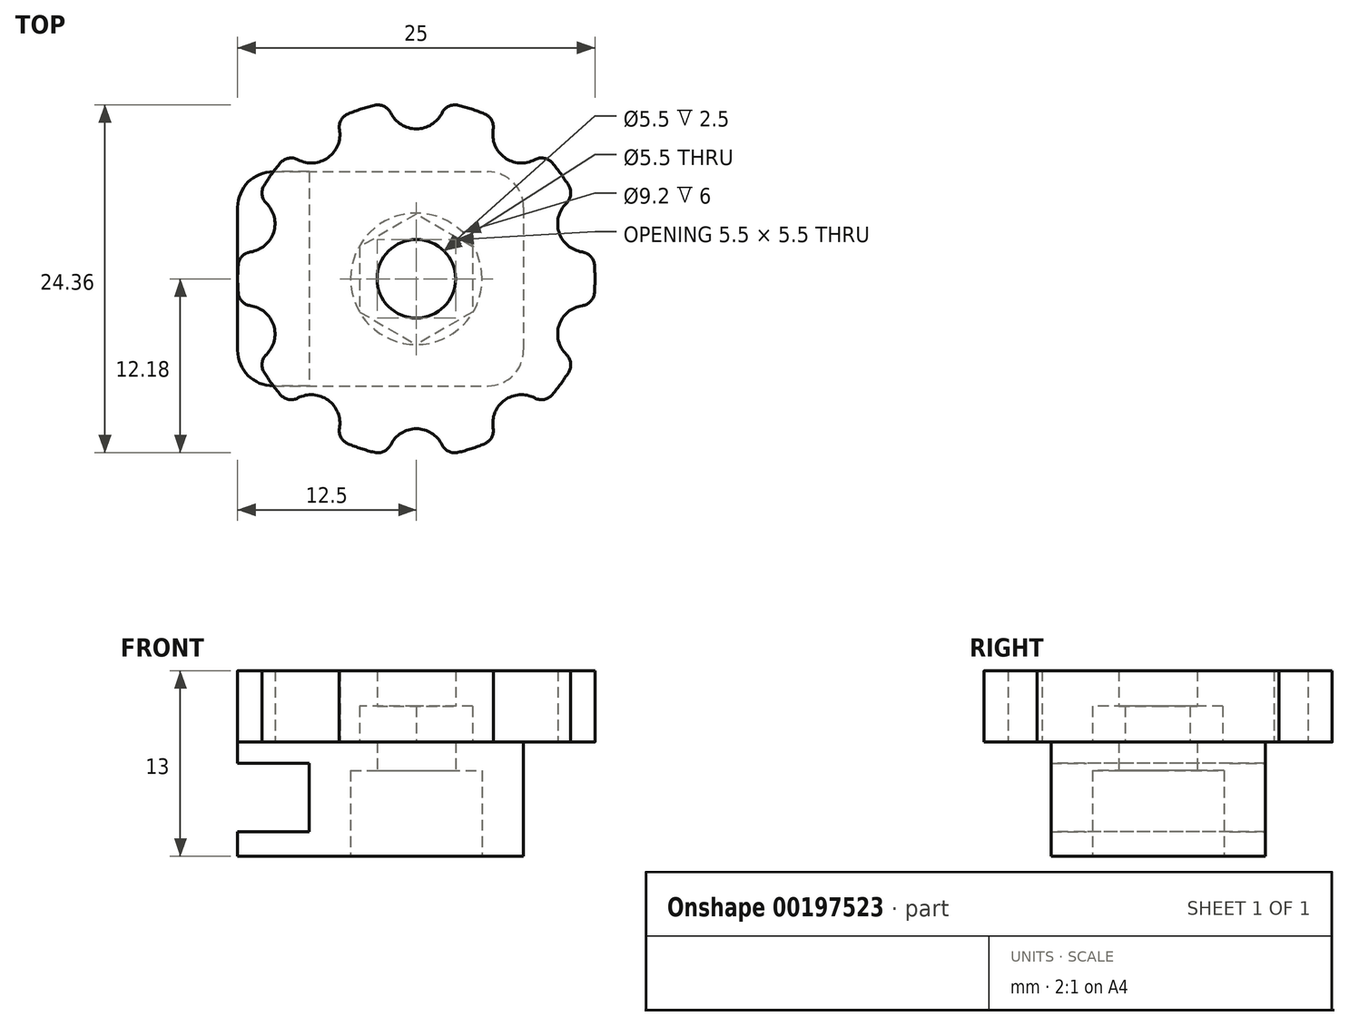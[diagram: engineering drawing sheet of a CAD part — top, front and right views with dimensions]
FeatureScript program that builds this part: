
annotation { "Feature Type Name" : "Feature", "Feature Type Description" : "" }
export const myFeature = defineFeature(function(context is Context, id is Id, definition is map)
    precondition{}
    {
        {
            var Q0;
            Q0=qCreatedBy(makeId("Top.planeOp"),FACE);
            var sketch = newSketch(context, id + "F0", { "sketchPlane" : qUnion([Q0])});
            skLineSegment(sketch, "E0.bottom", {"start": v(-12.5, 7.5) * mm, "end": v(7.5, 7.5) * mm});
            skLineSegment(sketch, "E0.top", {"start": v(-12.5, -7.5) * mm, "end": v(7.5, -7.5) * mm});
            skLineSegment(sketch, "E0.left", {"start": v(-12.5, 7.5) * mm, "end": v(-12.5, -7.5) * mm});
            skLineSegment(sketch, "E0.right", {"start": v(7.5, 7.5) * mm, "end": v(7.5, -7.5) * mm});
            skCircle(sketch, "E1", {"center": v(0, 0) * mm, "radius": 2.75 * mm});
            skSolve(sketch);
        }
        {
            var Q0;
            Q0=qSketchRegion(id+"F0",true);
            extrude(context, id + "F1", {"entities" : qUnion([Q0]), "depth" : 8 * mm});
        }
        {
            var Q0;
            Q0=makeQuery(id+"F1.opExtrude","SWEPT_FACE",FACE,{"disambiguationData":[OSD([sQuery(id+"F0.wireOp",EDGE,"E0.left")])]});
            var sketch = newSketch(context, id + "F2", { "sketchPlane" : qUnion([Q0])});
            skLineSegment(sketch, "E2.bottom", {"start": v(-7.5, 6.5) * mm, "end": v(7.5, 6.5) * mm});
            skLineSegment(sketch, "E2.top", {"start": v(-7.5, 1.7) * mm, "end": v(7.5, 1.7) * mm});
            skLineSegment(sketch, "E2.left", {"start": v(-7.5, 6.5) * mm, "end": v(-7.5, 1.7) * mm});
            skLineSegment(sketch, "E2.right", {"start": v(7.5, 6.5) * mm, "end": v(7.5, 1.7) * mm});
            skSolve(sketch);
        }
        {
            var Q0;
            Q0=qSketchRegion(id+"F2",true);
            extrude(context, id + "F3", {"entities" : qUnion([Q0]), "operationType" : NewBodyOperationType.REMOVE, "oppositeDirection" : true, "depth" : 5 * mm});
        }
        {
            var Q0;
            Q0=makeQuery(id+"F1.opExtrude","CAP_FACE",FACE,{"disambiguationData":[OSD([sQuery(id+"F0.wireOp",EDGE,"E0.bottom"),sQuery(id+"F0.wireOp",EDGE,"E0.top"),sQuery(id+"F0.wireOp",EDGE,"E0.left"),sQuery(id+"F0.wireOp",EDGE,"E0.right"),sQuery(id+"F0.wireOp",EDGE,"E1")])],"isStart":true});
            var sketch = newSketch(context, id + "F4", { "sketchPlane" : qUnion([Q0])});
            skCircle(sketch, "E3", {"center": v(0, 0) * mm, "radius": 4.6 * mm});
            skSolve(sketch);
        }
        {
            var Q0;
            Q0=qSketchRegion(id+"F4",true);
            extrude(context, id + "F5", {"entities" : qUnion([Q0]), "operationType" : NewBodyOperationType.REMOVE, "oppositeDirection" : true, "depth" : 6 * mm});
        }
        {
            var Q0;
            Q0=makeQuery(id+"F1.opExtrude","SWEPT_EDGE",EDGE,{"disambiguationData":[OSD([sQuery(id+"F0.wireOp",EDGE,"E0.top"),sQuery(id+"F0.wireOp",EDGE,"E0.right")])]});
            var Q1;
            Q1=makeQuery(id+"F1.opExtrude","SWEPT_EDGE",EDGE,{"disambiguationData":[OSD([sQuery(id+"F0.wireOp",EDGE,"E0.bottom"),sQuery(id+"F0.wireOp",EDGE,"E0.right")])]});
            fillet(context, id + "F6", {"entities" : qUnion([Q0, Q1]), "radius" : 2.5 * mm, "tangentPropagation" : true, "allowEdgeOverflow" : false});
        }
        {
            var Q0;
            {var subQ0=sQuery(id+"F0.wireOp",EDGE,"E0.left");var subQ1=sQuery(id+"F0.wireOp",EDGE,"E0.top");Q0=makeQuery(id+"F3.boolean.opBoolean","SPLIT",EDGE,{"disambiguationData":[TD([makeQuery(id+"F3.opExtrude","SWEPT_FACE",FACE,{"disambiguationData":[OSD([sQuery(id+"F2.wireOp",EDGE,"E2.top")])]})])],"derivedFrom":makeQuery(id+"F1.opExtrude","SWEPT_EDGE",EDGE,{"disambiguationData":[OSD([subQ1,subQ0])]})});}
            var Q1;
            {var subQ0=sQuery(id+"F0.wireOp",EDGE,"E0.left");var subQ1=sQuery(id+"F0.wireOp",EDGE,"E0.top");Q1=makeQuery(id+"F3.boolean.opBoolean","SPLIT",EDGE,{"disambiguationData":[TD([makeQuery(id+"F3.opExtrude","SWEPT_FACE",FACE,{"disambiguationData":[OSD([sQuery(id+"F2.wireOp",EDGE,"E2.bottom")])]})])],"derivedFrom":makeQuery(id+"F1.opExtrude","SWEPT_EDGE",EDGE,{"disambiguationData":[OSD([subQ1,subQ0])]})});}
            var Q2;
            {var subQ0=sQuery(id+"F0.wireOp",EDGE,"E0.bottom");var subQ1=sQuery(id+"F0.wireOp",EDGE,"E0.left");Q2=makeQuery(id+"F3.boolean.opBoolean","SPLIT",EDGE,{"disambiguationData":[TD([makeQuery(id+"F3.opExtrude","SWEPT_FACE",FACE,{"disambiguationData":[OSD([sQuery(id+"F2.wireOp",EDGE,"E2.top")])]})])],"derivedFrom":makeQuery(id+"F1.opExtrude","SWEPT_EDGE",EDGE,{"disambiguationData":[OSD([subQ0,subQ1])]})});}
            var Q3;
            {var subQ0=sQuery(id+"F0.wireOp",EDGE,"E0.bottom");var subQ1=sQuery(id+"F0.wireOp",EDGE,"E0.left");Q3=makeQuery(id+"F3.boolean.opBoolean","SPLIT",EDGE,{"disambiguationData":[TD([makeQuery(id+"F3.opExtrude","SWEPT_FACE",FACE,{"disambiguationData":[OSD([sQuery(id+"F2.wireOp",EDGE,"E2.bottom")])]})])],"derivedFrom":makeQuery(id+"F1.opExtrude","SWEPT_EDGE",EDGE,{"disambiguationData":[OSD([subQ0,subQ1])]})});}
            fillet(context, id + "F7", {"entities" : qUnion([Q0, Q1, Q2, Q3]), "radius" : 2.5 * mm, "tangentPropagation" : true, "allowEdgeOverflow" : false});
        }
        {
            var Q0;
            Q0=makeQuery(id+"F1.opExtrude","CAP_FACE",FACE,{"disambiguationData":[OSD([sQuery(id+"F0.wireOp",EDGE,"E0.bottom"),sQuery(id+"F0.wireOp",EDGE,"E0.top"),sQuery(id+"F0.wireOp",EDGE,"E0.left"),sQuery(id+"F0.wireOp",EDGE,"E0.right"),sQuery(id+"F0.wireOp",EDGE,"E1")])],"isStart":false});
            var sketch = newSketch(context, id + "F8", { "sketchPlane" : qUnion([Q0])});
            skArc(sketch, "E4", {"start": v(-2, 12.34) * mm, "mid": v(-3.86, 11.89) * mm, "end": v(-5.64, 11.16) * mm});
            skCircle(sketch, "E5.0", {"center": v(0, 0) * mm, "radius": 2.75 * mm});
            skArc(sketch, "E6", {"start": v(2, -12.34) * mm, "mid": v(0, -10.5) * mm, "end": v(-2, -12.34) * mm});
            skArc(sketch, "E7.1.0", {"start": v(8.87, -8.81) * mm, "mid": v(6.17, -8.5) * mm, "end": v(5.64, -11.16) * mm});
            skArc(sketch, "E7.2.0", {"start": v(12.35, -1.92) * mm, "mid": v(9.99, -3.24) * mm, "end": v(11.12, -5.7) * mm});
            skArc(sketch, "E7.3.0", {"start": v(11.12, 5.7) * mm, "mid": v(9.99, 3.24) * mm, "end": v(12.35, 1.92) * mm});
            skArc(sketch, "E7.4.0", {"start": v(5.64, 11.16) * mm, "mid": v(6.17, 8.5) * mm, "end": v(8.87, 8.81) * mm});
            skArc(sketch, "E7.5.0", {"start": v(-2, 12.34) * mm, "mid": v(0, 10.5) * mm, "end": v(2, 12.34) * mm});
            skArc(sketch, "E7.6.0", {"start": v(-8.87, 8.81) * mm, "mid": v(-6.17, 8.5) * mm, "end": v(-5.64, 11.16) * mm});
            skArc(sketch, "E7.7.0", {"start": v(-12.35, 1.92) * mm, "mid": v(-9.99, 3.24) * mm, "end": v(-11.12, 5.7) * mm});
            skArc(sketch, "E7.8.0", {"start": v(-11.12, -5.7) * mm, "mid": v(-9.99, -3.24) * mm, "end": v(-12.35, -1.92) * mm});
            skArc(sketch, "E7.9.0", {"start": v(-5.64, -11.16) * mm, "mid": v(-6.17, -8.5) * mm, "end": v(-8.87, -8.81) * mm});
            skArc(sketch, "E8.trimOffspring", {"start": v(5.64, 11.16) * mm, "mid": v(3.86, 11.89) * mm, "end": v(2, 12.34) * mm});
            skArc(sketch, "E9.trimOffspring", {"start": v(11.12, 5.7) * mm, "mid": v(10.11, 7.35) * mm, "end": v(8.87, 8.81) * mm});
            skArc(sketch, "E10.trimOffspring", {"start": v(12.35, -1.92) * mm, "mid": v(12.5, 0) * mm, "end": v(12.35, 1.92) * mm});
            skArc(sketch, "E11.trimOffspring", {"start": v(8.87, -8.81) * mm, "mid": v(10.11, -7.35) * mm, "end": v(11.12, -5.7) * mm});
            skArc(sketch, "E12.trimOffspring", {"start": v(2, -12.34) * mm, "mid": v(3.86, -11.89) * mm, "end": v(5.64, -11.16) * mm});
            skArc(sketch, "E13.trimOffspring", {"start": v(-5.64, -11.16) * mm, "mid": v(-3.86, -11.89) * mm, "end": v(-2, -12.34) * mm});
            skArc(sketch, "E14.trimOffspring", {"start": v(-11.12, -5.7) * mm, "mid": v(-10.11, -7.35) * mm, "end": v(-8.87, -8.81) * mm});
            skArc(sketch, "E15.trimOffspring", {"start": v(-12.35, 1.92) * mm, "mid": v(-12.5, 0) * mm, "end": v(-12.35, -1.92) * mm});
            skArc(sketch, "E16.trimOffspring", {"start": v(-8.87, 8.81) * mm, "mid": v(-10.11, 7.35) * mm, "end": v(-11.12, 5.7) * mm});
            skSolve(sketch);
        }
        {
            var Q0;
            Q0=qSketchRegion(id+"F8",true);
            extrude(context, id + "F9", {"entities" : qUnion([Q0]), "depth" : 5 * mm});
        }
        {
            var Q0;
            Q0=makeQuery(id+"F9.opExtrude","SWEPT_EDGE",EDGE,{"disambiguationData":[OSD([sQuery(id+"F8.wireOp",EDGE,"E7.9.0"),sQuery(id+"F8.wireOp",EDGE,"E14.trimOffspring")])]});
            var Q1;
            Q1=makeQuery(id+"F9.opExtrude","SWEPT_EDGE",EDGE,{"disambiguationData":[OSD([sQuery(id+"F8.wireOp",EDGE,"E7.9.0"),sQuery(id+"F8.wireOp",EDGE,"E13.trimOffspring")])]});
            var Q2;
            Q2=makeQuery(id+"F9.opExtrude","SWEPT_EDGE",EDGE,{"disambiguationData":[OSD([sQuery(id+"F8.wireOp",EDGE,"E6"),sQuery(id+"F8.wireOp",EDGE,"E13.trimOffspring")])]});
            var Q3;
            Q3=makeQuery(id+"F9.opExtrude","SWEPT_EDGE",EDGE,{"disambiguationData":[OSD([sQuery(id+"F8.wireOp",EDGE,"E6"),sQuery(id+"F8.wireOp",EDGE,"E12.trimOffspring")])]});
            var Q4;
            Q4=makeQuery(id+"F9.opExtrude","SWEPT_EDGE",EDGE,{"disambiguationData":[OSD([sQuery(id+"F8.wireOp",EDGE,"E7.1.0"),sQuery(id+"F8.wireOp",EDGE,"E12.trimOffspring")])]});
            var Q5;
            Q5=makeQuery(id+"F9.opExtrude","SWEPT_EDGE",EDGE,{"disambiguationData":[OSD([sQuery(id+"F8.wireOp",EDGE,"E7.1.0"),sQuery(id+"F8.wireOp",EDGE,"E11.trimOffspring")])]});
            var Q6;
            Q6=makeQuery(id+"F9.opExtrude","SWEPT_EDGE",EDGE,{"disambiguationData":[OSD([sQuery(id+"F8.wireOp",EDGE,"E7.2.0"),sQuery(id+"F8.wireOp",EDGE,"E11.trimOffspring")])]});
            var Q7;
            Q7=makeQuery(id+"F9.opExtrude","SWEPT_EDGE",EDGE,{"disambiguationData":[OSD([sQuery(id+"F8.wireOp",EDGE,"E7.2.0"),sQuery(id+"F8.wireOp",EDGE,"E10.trimOffspring")])]});
            var Q8;
            Q8=makeQuery(id+"F9.opExtrude","SWEPT_EDGE",EDGE,{"disambiguationData":[OSD([sQuery(id+"F8.wireOp",EDGE,"E7.3.0"),sQuery(id+"F8.wireOp",EDGE,"E10.trimOffspring")])]});
            var Q9;
            Q9=makeQuery(id+"F9.opExtrude","SWEPT_EDGE",EDGE,{"disambiguationData":[OSD([sQuery(id+"F8.wireOp",EDGE,"E7.3.0"),sQuery(id+"F8.wireOp",EDGE,"E9.trimOffspring")])]});
            var Q10;
            Q10=makeQuery(id+"F9.opExtrude","SWEPT_EDGE",EDGE,{"disambiguationData":[OSD([sQuery(id+"F8.wireOp",EDGE,"E7.4.0"),sQuery(id+"F8.wireOp",EDGE,"E9.trimOffspring")])]});
            var Q11;
            Q11=makeQuery(id+"F9.opExtrude","SWEPT_EDGE",EDGE,{"disambiguationData":[OSD([sQuery(id+"F8.wireOp",EDGE,"E7.4.0"),sQuery(id+"F8.wireOp",EDGE,"E8.trimOffspring")])]});
            var Q12;
            Q12=makeQuery(id+"F9.opExtrude","SWEPT_EDGE",EDGE,{"disambiguationData":[OSD([sQuery(id+"F8.wireOp",EDGE,"E7.8.0"),sQuery(id+"F8.wireOp",EDGE,"E15.trimOffspring")])]});
            var Q13;
            Q13=makeQuery(id+"F9.opExtrude","SWEPT_EDGE",EDGE,{"disambiguationData":[OSD([sQuery(id+"F8.wireOp",EDGE,"E7.8.0"),sQuery(id+"F8.wireOp",EDGE,"E14.trimOffspring")])]});
            var Q14;
            Q14=makeQuery(id+"F9.opExtrude","SWEPT_EDGE",EDGE,{"disambiguationData":[OSD([sQuery(id+"F8.wireOp",EDGE,"E7.7.0"),sQuery(id+"F8.wireOp",EDGE,"E15.trimOffspring")])]});
            var Q15;
            Q15=makeQuery(id+"F9.opExtrude","SWEPT_EDGE",EDGE,{"disambiguationData":[OSD([sQuery(id+"F8.wireOp",EDGE,"E7.7.0"),sQuery(id+"F8.wireOp",EDGE,"E16.trimOffspring")])]});
            var Q16;
            Q16=makeQuery(id+"F9.opExtrude","SWEPT_EDGE",EDGE,{"disambiguationData":[OSD([sQuery(id+"F8.wireOp",EDGE,"E7.5.0"),sQuery(id+"F8.wireOp",EDGE,"E8.trimOffspring")])]});
            var Q17;
            Q17=makeQuery(id+"F9.opExtrude","SWEPT_EDGE",EDGE,{"disambiguationData":[OSD([sQuery(id+"F8.wireOp",EDGE,"E4"),sQuery(id+"F8.wireOp",EDGE,"E7.5.0")])]});
            var Q18;
            Q18=makeQuery(id+"F9.opExtrude","SWEPT_EDGE",EDGE,{"disambiguationData":[OSD([sQuery(id+"F8.wireOp",EDGE,"E4"),sQuery(id+"F8.wireOp",EDGE,"E7.6.0")])]});
            var Q19;
            Q19=makeQuery(id+"F9.opExtrude","SWEPT_EDGE",EDGE,{"disambiguationData":[OSD([sQuery(id+"F8.wireOp",EDGE,"E7.6.0"),sQuery(id+"F8.wireOp",EDGE,"E16.trimOffspring")])]});
            fillet(context, id + "F10", {"entities" : qUnion([Q0, Q1, Q2, Q3, Q4, Q5, Q6, Q7, Q8, Q9, Q10, Q11, Q12, Q13, Q14, Q15, Q16, Q17, Q18, Q19]), "radius" : 1 * mm, "tangentPropagation" : true, "allowEdgeOverflow" : false});
        }
        {
            var Q0;
            Q0=makeQuery(id+"F9.opExtrude","CAP_FACE",FACE,{"disambiguationData":[OSD([sQuery(id+"F8.wireOp",EDGE,"E4"),sQuery(id+"F8.wireOp",EDGE,"E5.0")])],"isStart":true});
            var sketch = newSketch(context, id + "F11", { "sketchPlane" : qUnion([Q0])});
            skCircle(sketch, "E17", {"center": v(0, 0.04) * mm, "radius": 3.95 * mm, "construction": true});
            skLineSegment(sketch, "E18", {"start": v(0, -6.7) * mm, "end": v(0, 9.73) * mm, "construction": true});
            skLineSegment(sketch, "E19", {"start": v(-6.74, 0.04) * mm, "end": v(6.08, 0.04) * mm, "construction": true});
            skLineSegment(sketch, "E20", {"start": v(-3.96, -2.24) * mm, "end": v(-3.96, 2.32) * mm});
            skLineSegment(sketch, "E21", {"start": v(-3.96, 2.32) * mm, "end": v(0, 4.6) * mm});
            skLineSegment(sketch, "E22", {"start": v(3.94, -2.24) * mm, "end": v(0, -4.52) * mm});
            skLineSegment(sketch, "E23", {"start": v(0, -4.52) * mm, "end": v(-3.96, -2.24) * mm});
            skLineSegment(sketch, "E24", {"start": v(3.94, -2.24) * mm, "end": v(3.94, 2.32) * mm});
            skLineSegment(sketch, "E25", {"start": v(3.94, 2.32) * mm, "end": v(0, 4.6) * mm});
            skSolve(sketch);
        }
        {
            var Q0;
            Q0=qSketchRegion(id+"F11",true);
            extrude(context, id + "F12", {"entities" : qUnion([Q0]), "operationType" : NewBodyOperationType.REMOVE, "oppositeDirection" : true, "depth" : 2.5 * mm});
        }
    });
